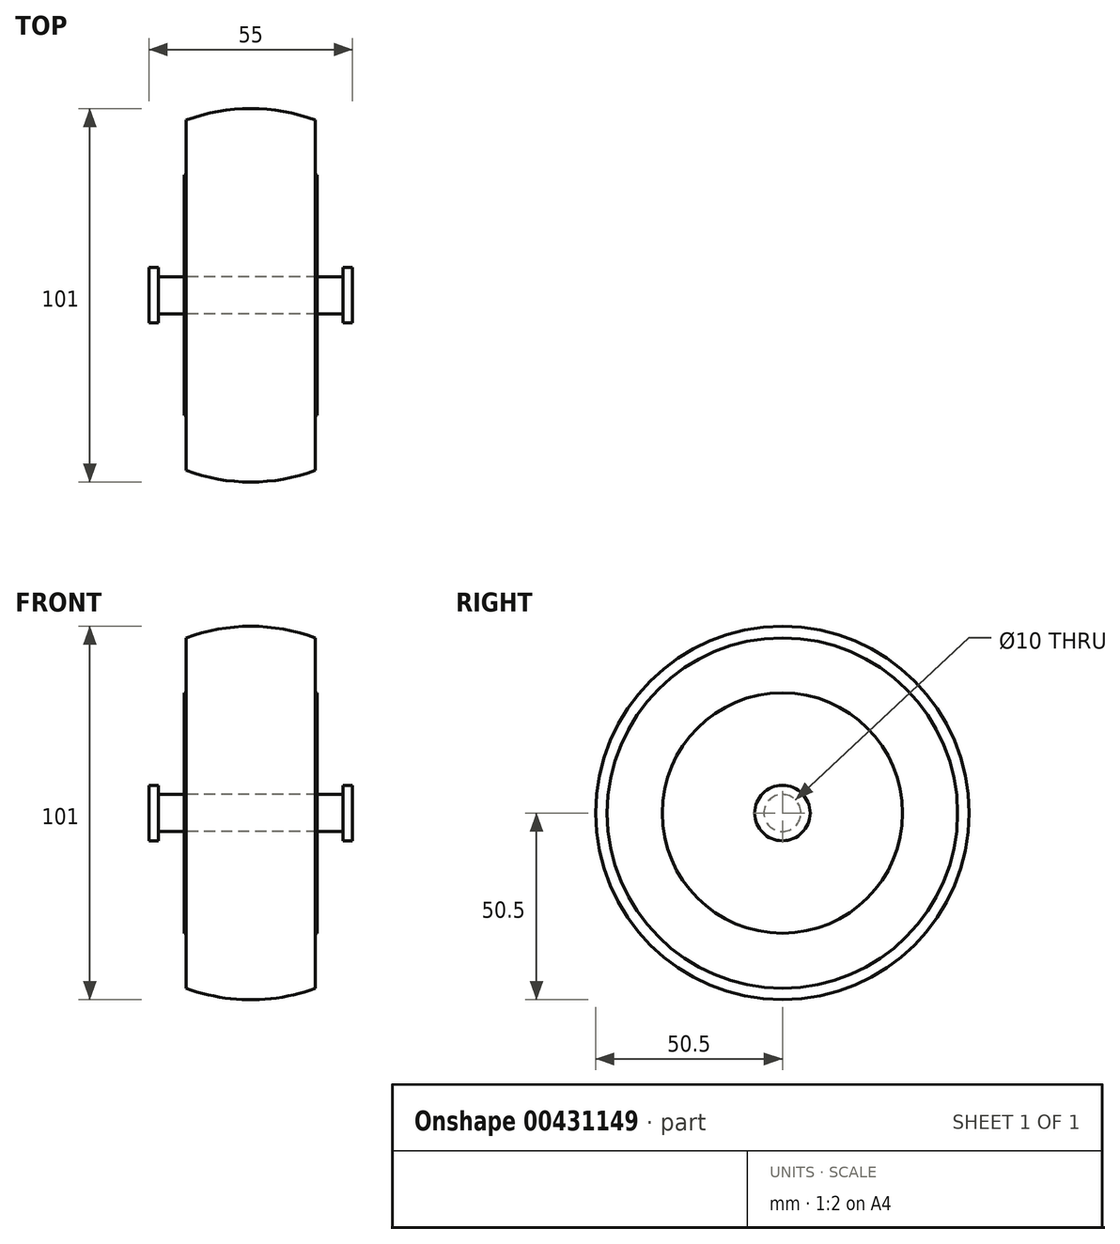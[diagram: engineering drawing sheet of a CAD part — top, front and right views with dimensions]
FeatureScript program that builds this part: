
annotation { "Feature Type Name" : "Feature", "Feature Type Description" : "" }
export const myFeature = defineFeature(function(context is Context, id is Id, definition is map)
    precondition{}
    {
        {
            var Q0;
            Q0=qCreatedBy(makeId("Right.planeOp"),FACE);
            var sketch = newSketch(context, id + "F0", { "sketchPlane" : qUnion([Q0])});
            skCircle(sketch, "E0", {"center": v(0, 0) * mm, "radius": 50.5 * mm});
            skCircle(sketch, "E1", {"center": v(0, 0) * mm, "radius": 35 * mm});
            skCircle(sketch, "E2", {"center": v(0, 0) * mm, "radius": 32.5 * mm});
            skCircle(sketch, "E3", {"center": v(0, 0) * mm, "radius": 5 * mm});
            skLineSegment(sketch, "E4", {"start": v(0, 0) * mm, "end": v(0, 50.5) * mm});
            skSolve(sketch);
        }
        {
            var Q0;
            Q0=makeQuery(id+"F0.imprint","IMPRINT",FACE,{"disambiguationData":[TD([[makeQuery(id+"F0.imprint","IMPRINT",EDGE,{"derivedFrom":sQuery(id+"F0.wireOp",EDGE,"E1")}),1.0]])]});
            var Q1;
            Q1=makeQuery(id+"F0.imprint","IMPRINT",FACE,{"disambiguationData":[TD([[makeQuery(id+"F0.imprint","IMPRINT",EDGE,{"derivedFrom":sQuery(id+"F0.wireOp",EDGE,"E2")}),1.0]])]});
            var Q2;
            Q2=makeQuery(id+"F0.imprint","IMPRINT",FACE,{"disambiguationData":[TD([[makeQuery(id+"F0.imprint","IMPRINT",EDGE,{"derivedFrom":sQuery(id+"F0.wireOp",EDGE,"E0")}),1.0]])]});
            extrude(context, id + "F1", {"entities" : qUnion([Q0, Q1, Q2]), "endBound" : BoundingType.SYMMETRIC, "depth" : 35 * mm});
        }
        {
            var Q0;
            Q0=makeQuery(id+"F0.imprint","IMPRINT",FACE,{"disambiguationData":[TD([[makeQuery(id+"F0.imprint","IMPRINT",EDGE,{"derivedFrom":sQuery(id+"F0.wireOp",EDGE,"E2")}),1.0]])]});
            var Q1;
            Q1 = qSketchRegion(id + "F3", true);
            extrude(context, id + "F2", {"entities" : qUnion([Q0, Q1]), "operationType" : NewBodyOperationType.ADD, "endBound" : BoundingType.SYMMETRIC, "depth" : 36 * mm});
        }
        {
            var Q0;
            Q0=qCreatedBy(makeId("Front.planeOp"),FACE);
            var sketch = newSketch(context, id + "F3", { "sketchPlane" : qUnion([Q0])});
            skLineSegment(sketch, "E5", {"start": v(0, 0) * mm, "end": v(0, 50.5) * mm, "construction": true});
            skLineSegment(sketch, "E6", {"start": v(-51.6, 0) * mm, "end": v(51.36, 0) * mm, "construction": true});
            skLineSegment(sketch, "E7", {"start": v(0, 50.5) * mm, "end": v(-17.5, 50.5) * mm});
            skLineSegment(sketch, "E8", {"start": v(-17.5, 47.37) * mm, "end": v(-17.5, 50.5) * mm});
            skLineSegment(sketch, "E9.MirrorCS", {"start": v(0, 50.5) * mm, "end": v(17.5, 50.5) * mm});
            skLineSegment(sketch, "E10.MirrorCS", {"start": v(17.5, 47.37) * mm, "end": v(17.5, 50.5) * mm});
            skArc(sketch, "E11.trimOffspring", {"start": v(17.5, 47.37) * mm, "mid": v(0, 50.5) * mm, "end": v(-17.5, 47.37) * mm});
            skPoint(sketch, "E12.MirrorCS.end.orphan", {"position": v(17.5, 43.45) * mm});
            skPoint(sketch, "E12.MirrorCS.start.orphan", {"position": v(0, 50.5) * mm});
            skPoint(sketch, "E13.center.orphan", {"position": v(0, 25.25) * mm});
            skPoint(sketch, "E14.orphan", {"position": v(-17.5, 43.45) * mm});
            skSolve(sketch);
        }
        {
            var Q0;
            Q0=qSketchRegion(id+"F3",true);
            var Q1;
            Q1=sQuery(id+"F3.wireOp",EDGE,"E6");
            revolve(context, id + "F4", {"operationType" : NewBodyOperationType.REMOVE, "entities" : qUnion([Q0]), "axis" : qUnion([Q1]), "revolveType" : RevolveType.FULL, "oppositeDirection" : true});
        }
        {
            var Q0;
            Q0=makeQuery(id+"F0.imprint","IMPRINT",FACE,{"disambiguationData":[TD([[makeQuery(id+"F0.imprint","IMPRINT",EDGE,{"derivedFrom":sQuery(id+"F0.wireOp",EDGE,"E3")}),1.0]])]});
            extrude(context, id + "F5", {"entities" : qUnion([Q0]), "endBound" : BoundingType.SYMMETRIC, "depth" : 50 * mm});
        }
        {
            var Q0;
            Q0=makeQuery(id+"F5.opExtrude","CAP_FACE",FACE,{"disambiguationData":[OSD([sQuery(id+"F0.wireOp",EDGE,"E3")])],"isStart":false});
            var sketch = newSketch(context, id + "F6", { "sketchPlane" : qUnion([Q0])});
            skCircle(sketch, "E15", {"center": v(0, 0) * mm, "radius": 7.5 * mm});
            skSolve(sketch);
        }
        {
            var Q0;
            Q0=makeQuery(id+"F6.imprint","IMPRINT",FACE,{"disambiguationData":[TD([[makeQuery(id+"F6.imprint","IMPRINT",EDGE,{"derivedFrom":sQuery(id+"F6.wireOp",EDGE,"E15")}),1.0]])]});
            var Q1;
            Q1=makeQuery(id+"F6.imprint","IMPRINT",FACE,{"disambiguationData":[TD([[makeQuery(id+"F6.imprint","IMPRINT",EDGE,{"derivedFrom":makeQuery(id+"F5.opExtrude","CAP_EDGE",EDGE,{"disambiguationData":[OSD([sQuery(id+"F0.wireOp",EDGE,"E3")])],"isStart":false})}),1.0]])]});
            extrude(context, id + "F7", {"entities" : qUnion([Q0, Q1]), "operationType" : NewBodyOperationType.ADD, "depth" : 2.5 * mm});
        }
        {
            var Q0;
            Q0=makeQuery(id+"F5.opExtrude","CAP_FACE",FACE,{"disambiguationData":[OSD([sQuery(id+"F0.wireOp",EDGE,"E3")])],"isStart":true});
            var sketch = newSketch(context, id + "F8", { "sketchPlane" : qUnion([Q0])});
            skCircle(sketch, "E16", {"center": v(0, 0) * mm, "radius": 7.5 * mm});
            skSolve(sketch);
        }
        {
            var Q0;
            Q0=makeQuery(id+"F8.imprint","IMPRINT",FACE,{"disambiguationData":[TD([[makeQuery(id+"F8.imprint","IMPRINT",EDGE,{"derivedFrom":makeQuery(id+"F5.opExtrude","CAP_EDGE",EDGE,{"disambiguationData":[OSD([sQuery(id+"F0.wireOp",EDGE,"E3")])],"isStart":true})}),-1.0]])]});
            var Q1;
            Q1=makeQuery(id+"F8.imprint","IMPRINT",FACE,{"disambiguationData":[TD([[makeQuery(id+"F8.imprint","IMPRINT",EDGE,{"derivedFrom":sQuery(id+"F8.wireOp",EDGE,"E16")}),1.0]])]});
            extrude(context, id + "F9", {"entities" : qUnion([Q0, Q1]), "operationType" : NewBodyOperationType.ADD, "depth" : 2.5 * mm});
        }
    });
